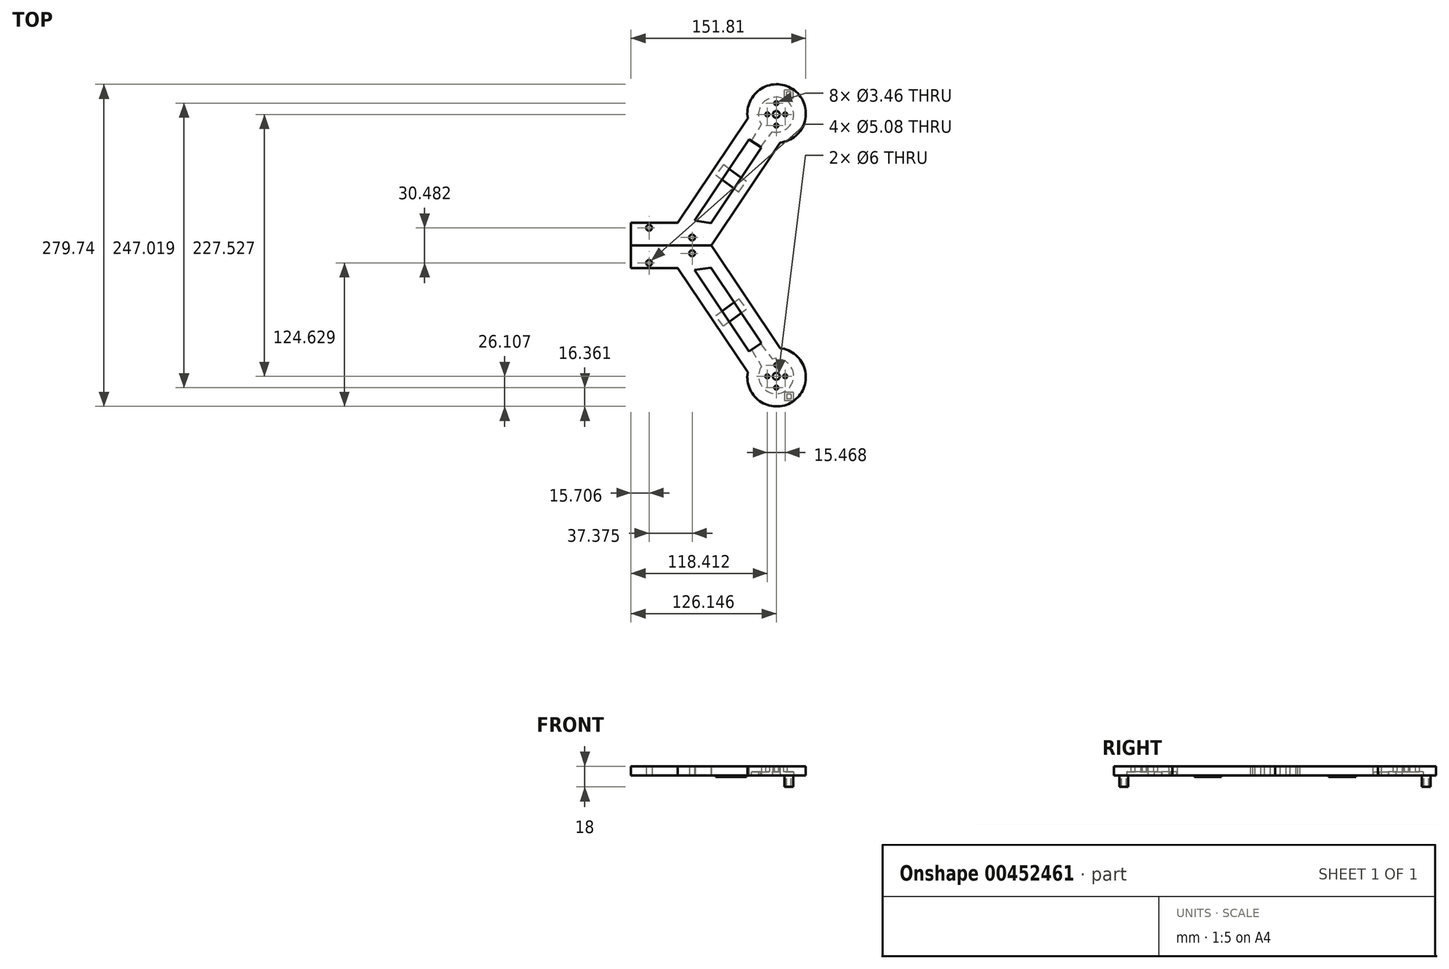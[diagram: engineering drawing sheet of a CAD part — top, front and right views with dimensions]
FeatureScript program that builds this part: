
annotation { "Feature Type Name" : "Feature", "Feature Type Description" : "" }
export const myFeature = defineFeature(function(context is Context, id is Id, definition is map)
    precondition{}
    {
        {
            var Q0;
            Q0=qCreatedBy(makeId("Top.planeOp"),FACE);
            var sketch = newSketch(context, id + "F0", { "sketchPlane" : qUnion([Q0])});
            skLineSegment(sketch, "E0.bottom", {"start": v(0, 0) * mm, "end": v(40.64, 0) * mm});
            skLineSegment(sketch, "E0.top", {"start": v(0, -19.57) * mm, "end": v(40.64, -19.57) * mm});
            skLineSegment(sketch, "E0.left", {"start": v(0, 0) * mm, "end": v(0, -19.57) * mm});
            skLineSegment(sketch, "E0.right", {"start": v(40.64, 0) * mm, "end": v(40.64, -19.57) * mm});
            skLineSegment(sketch, "E1", {"start": v(69.71, 0) * mm, "end": v(40.64, 0) * mm});
            skLineSegment(sketch, "E2", {"start": v(69.71, 0) * mm, "end": v(137.47, -101.36) * mm});
            skLineSegment(sketch, "E3", {"start": v(40.64, -19.57) * mm, "end": v(101.34, -110.37) * mm});
            skLineSegment(sketch, "E4", {"start": v(113.23, -84.95) * mm, "end": v(69.47, -19.49) * mm});
            skLineSegment(sketch, "E5", {"start": v(113.23, -84.95) * mm, "end": v(102.41, -92.18) * mm});
            skLineSegment(sketch, "E6", {"start": v(102.41, -92.18) * mm, "end": v(55.12, -21.44) * mm});
            skLineSegment(sketch, "E7", {"start": v(55.12, -21.44) * mm, "end": v(69.47, -19.49) * mm});
            skCircle(sketch, "E8", {"center": v(126.4, -114.47) * mm, "radius": 25.4 * mm});
            skSolve(sketch);
        }
        {
            var Q0;
            Q0=qSketchRegion(id+"F0",true);
            extrude(context, id + "F1", {"entities" : qUnion([Q0]), "depth" : 8 * mm, "offsetDistance" : 25 * mm});
        }
        {
            var Q0;
            Q0=qCreatedBy(makeId("Top.planeOp"),FACE);
            var sketch = newSketch(context, id + "F2", { "sketchPlane" : qUnion([Q0])});
            skPoint(sketch, "E9.middle", {"position": v(0, 0) * mm});
            skCircle(sketch, "E10", {"center": v(15.7, -15.24) * mm, "radius": 2.54 * mm});
            skCircle(sketch, "E11", {"center": v(126.15, -113.76) * mm, "radius": 3 * mm});
            skLineSegment(sketch, "E12", {"start": v(126.15, -113.76) * mm, "end": v(126.15, -104.02) * mm});
            skLineSegment(sketch, "E13", {"start": v(118.41, -113.76) * mm, "end": v(126.15, -113.76) * mm});
            skLineSegment(sketch, "E14", {"start": v(126.15, -113.76) * mm, "end": v(133.88, -113.76) * mm});
            skLineSegment(sketch, "E15", {"start": v(126.15, -113.76) * mm, "end": v(126.15, -123.5) * mm});
            skCircle(sketch, "E16", {"center": v(133.88, -113.76) * mm, "radius": 1.73 * mm});
            skCircle(sketch, "E17", {"center": v(126.15, -123.5) * mm, "radius": 1.73 * mm});
            skCircle(sketch, "E18", {"center": v(118.41, -113.76) * mm, "radius": 1.73 * mm});
            skCircle(sketch, "E19", {"center": v(126.15, -104.02) * mm, "radius": 1.73 * mm});
            skCircle(sketch, "E20", {"center": v(53.08, -6.87) * mm, "radius": 2.54 * mm});
            skSolve(sketch);
        }
        {
            var Q0;
            Q0=qSketchRegion(id+"F2",true);
            extrude(context, id + "F3", {"entities" : qUnion([Q0]), "operationType" : NewBodyOperationType.REMOVE, "depth" : 101.85 * mm});
        }
        {
            var Q0;
            Q0=qCreatedBy(makeId("Top.planeOp"),FACE);
            var sketch = newSketch(context, id + "F4", { "sketchPlane" : qUnion([Q0])});
            skCircle(sketch, "E21", {"center": v(125.97, -113.53) * mm, "radius": 15.24 * mm});
            skLineSegment(sketch, "E22", {"start": v(112.12, -84.85) * mm, "end": v(122.67, -98.65) * mm});
            skLineSegment(sketch, "E23", {"start": v(104.28, -90.05) * mm, "end": v(113.38, -105.03) * mm});
            skLineSegment(sketch, "E24", {"start": v(113.38, -105.03) * mm, "end": v(122.67, -98.65) * mm});
            skLineSegment(sketch, "E25", {"start": v(104.28, -90.05) * mm, "end": v(112.12, -84.85) * mm});
            skSolve(sketch);
        }
        {
            var Q0;
            Q0=qSketchRegion(id+"F4",true);
            extrude(context, id + "F5", {"entities" : qUnion([Q0]), "operationType" : NewBodyOperationType.REMOVE, "depth" : 3 * mm, "offsetDistance" : 25.4 * mm});
        }
        {
            var Q0;
            Q0=qCreatedBy(makeId("Top.planeOp"),FACE);
            var sketch = newSketch(context, id + "F6", { "sketchPlane" : qUnion([Q0])});
            skLineSegment(sketch, "E26", {"start": v(80.1, -70.2) * mm, "end": v(73.51, -61.09) * mm});
            skLineSegment(sketch, "E27", {"start": v(73.51, -61.09) * mm, "end": v(93.69, -46.48) * mm});
            skLineSegment(sketch, "E28", {"start": v(93.69, -46.48) * mm, "end": v(100.28, -55.58) * mm});
            skLineSegment(sketch, "E29", {"start": v(100.28, -55.58) * mm, "end": v(80.1, -70.2) * mm});
            skSolve(sketch);
        }
        {
            var Q0;
            Q0=qSketchRegion(id+"F6",true);
            extrude(context, id + "F7", {"entities" : qUnion([Q0]), "operationType" : NewBodyOperationType.ADD, "oppositeDirection" : true, "depth" : 1.27 * mm});
        }
        {
            var Q0;
            Q0=makeQuery(id+"F1.opExtrude","CAP_FACE",FACE,{"disambiguationData":[OSD([sQuery(id+"F0.wireOp",EDGE,"E0.bottom"),sQuery(id+"F0.wireOp",EDGE,"E0.top"),sQuery(id+"F0.wireOp",EDGE,"E0.left"),sQuery(id+"F0.wireOp",EDGE,"E1"),sQuery(id+"F0.wireOp",EDGE,"E2"),sQuery(id+"F0.wireOp",EDGE,"E3"),sQuery(id+"F0.wireOp",EDGE,"E4"),sQuery(id+"F0.wireOp",EDGE,"E5"),sQuery(id+"F0.wireOp",EDGE,"E6"),sQuery(id+"F0.wireOp",EDGE,"E7"),sQuery(id+"F0.wireOp",EDGE,"E8")])],"isStart":true});
            var sketch = newSketch(context, id + "F8", { "sketchPlane" : qUnion([Q0])});
            skLineSegment(sketch, "E30.bottom", {"start": v(140.83, 127.54) * mm, "end": v(133.33, 127.54) * mm});
            skLineSegment(sketch, "E30.top", {"start": v(140.83, 135.04) * mm, "end": v(133.33, 135.04) * mm});
            skLineSegment(sketch, "E30.left", {"start": v(140.83, 127.54) * mm, "end": v(140.83, 135.04) * mm});
            skLineSegment(sketch, "E30.right", {"start": v(133.33, 127.54) * mm, "end": v(133.33, 135.04) * mm});
            skPoint(sketch, "E30.middle", {"position": v(137.08, 131.29) * mm});
            skLineSegment(sketch, "E31.bottom", {"start": v(139.08, 129.29) * mm, "end": v(135.08, 129.29) * mm});
            skLineSegment(sketch, "E31.top", {"start": v(139.08, 133.29) * mm, "end": v(135.08, 133.29) * mm});
            skLineSegment(sketch, "E31.left", {"start": v(139.08, 129.29) * mm, "end": v(139.08, 133.29) * mm});
            skLineSegment(sketch, "E31.right", {"start": v(135.08, 129.29) * mm, "end": v(135.08, 133.29) * mm});
            skSolve(sketch);
        }
        {
            var Q0;
            Q0=makeQuery(id+"F8.imprint","IMPRINT",FACE,{"disambiguationData":[TD([[makeQuery(id+"F8.imprint","IMPRINT",EDGE,{"derivedFrom":sQuery(id+"F8.wireOp",EDGE,"E30.bottom")}),-1.0]])]});
            extrude(context, id + "F9", {"entities" : qUnion([Q0]), "operationType" : NewBodyOperationType.ADD, "depth" : 10 * mm, "offsetDistance" : 25 * mm});
        }
        {
            var Q0;
            Q0=makeQuery(id+"F1.opExtrude","SWEPT_BODY",BODY,{"disambiguationData":[OSD([sQuery(id+"F0.wireOp",EDGE,"E0.bottom"),sQuery(id+"F0.wireOp",EDGE,"E0.top"),sQuery(id+"F0.wireOp",EDGE,"E0.left"),sQuery(id+"F0.wireOp",EDGE,"E1"),sQuery(id+"F0.wireOp",EDGE,"E2"),sQuery(id+"F0.wireOp",EDGE,"E3"),sQuery(id+"F0.wireOp",EDGE,"E4"),sQuery(id+"F0.wireOp",EDGE,"E5"),sQuery(id+"F0.wireOp",EDGE,"E6"),sQuery(id+"F0.wireOp",EDGE,"E7"),sQuery(id+"F0.wireOp",EDGE,"E8")])]});
            var Q1;
            Q1=makeQuery(id+"F1.opExtrude","SWEPT_FACE",FACE,{"disambiguationData":[OSD([sQuery(id+"F0.wireOp",EDGE,"E0.bottom"),sQuery(id+"F0.wireOp",EDGE,"E1")])]});
            mirror(context, id + "F10", {"entities" : qUnion([Q0]), "mirrorPlane" : qUnion([Q1])});
        }
    });
